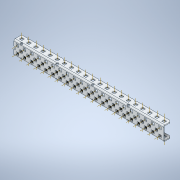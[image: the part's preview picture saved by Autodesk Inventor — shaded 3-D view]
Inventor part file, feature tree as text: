
AUTODESK INVENTOR PART (.ipt)
format: ipt  version: 2020 (Build 240168000, 168)  size: 1,398,784 bytes
history: native  units: in
note: dims shown in document units (in); Inventor stores cm internally (conversion verified against a paired STEP export)
features: other x108, plane x8, pattern_linear x4, split x2, sheet_metal_op x1
ambient origin geometry x8: Origin, YZ Plane, XZ Plane, XY Plane, X Axis, Y Axis, Z Axis, Center Point
bodies: Solid1 (feature_tree)
feature tree (123):
  other  "Work Axis1"
  pattern_linear  "Rectangular Pattern1"  Count1=21 Spacing1=0.5in
  other  "Work Axis72"
  pattern_linear  "Rectangular Pattern2"  Count1=21 Spacing1=0.5in
  pattern_linear  "Rectangular Pattern3"  Count1=21 Spacing1=0.5in
  other  "Work Axis141"
  pattern_linear  "Rectangular Pattern4"  Count1=20 Spacing1=0.5in
  plane  "Work Plane7"
  split  "Split1"
  plane  "Work Plane8"
  split  "Split2"
  plane  "Work Plane1"
  plane  "Work Plane2"
  other  "Work Point1"
  other  "Work Axis2"
  other  "Work Axis3"
  other  "Work Axis4"
  other  "Work Axis5"
  other  "Work Axis6"
  other  "Work Axis7"
  other  "Work Axis8"
  other  "Work Axis9"
  other  "Work Axis10"
  other  "Work Axis11"
  other  "Work Axis12"
  other  "Work Axis13"
  other  "Work Axis14"
  other  "Work Axis15"
  other  "Work Axis16"
  other  "Work Axis17"
  other  "Work Axis18"
  other  "Work Axis19"
  other  "Work Axis20"
  other  "Work Axis21"
  other  "Work Axis36"
  other  "Work Axis37"
  other  "Work Axis38"
  other  "Work Axis39"
  other  "Work Axis40"
  other  "Work Axis41"
  other  "Work Axis42"
  other  "Work Axis43"
  other  "Work Axis44"
  other  "Work Axis45"
  other  "Work Axis46"
  other  "Work Axis47"
  other  "Work Axis48"
  other  "Work Axis49"
  other  "Work Axis50"
  other  "Work Axis51"
  other  "Work Axis52"
  other  "Work Axis53"
  other  "Work Axis54"
  other  "Work Axis55"
  other  "Work Axis56"
  plane  "Work Plane3"
  plane  "Work Plane4"
  other  "Work Point2"
  other  "Work Axis71"
  other  "Work Point3"
  other  "Work Axis73"
  other  "Work Axis74"
  other  "Work Axis75"
  other  "Work Axis76"
  other  "Work Axis77"
  other  "Work Axis78"
  other  "Work Axis79"
  other  "Work Axis80"
  other  "Work Axis81"
  other  "Work Axis82"
  other  "Work Axis83"
  other  "Work Axis84"
  other  "Work Axis85"
  other  "Work Axis86"
  other  "Work Axis87"
  other  "Work Axis88"
  other  "Work Axis89"
  other  "Work Axis90"
  other  "Work Axis91"
  other  "Work Axis92"
  other  "Work Axis107"
  other  "Work Axis108"
  other  "Work Axis109"
  other  "Work Axis110"
  other  "Work Axis111"
  other  "Work Axis112"
  other  "Work Axis113"
  other  "Work Axis114"
  other  "Work Axis115"
  other  "Work Axis116"
  other  "Work Axis117"
  other  "Work Axis118"
  other  "Work Axis119"
  other  "Work Axis120"
  other  "Work Axis121"
  other  "Work Axis122"
  other  "Work Axis123"
  other  "Work Axis124"
  other  "Work Axis125"
  other  "Work Axis126"
  plane  "Work Plane5"
  plane  "Work Plane6"
  other  "Work Point4"
  other  "Work Axis142"
  other  "Work Axis143"
  other  "Work Axis144"
  other  "Work Axis145"
  other  "Work Axis146"
  other  "Work Axis147"
  other  "Work Axis148"
  other  "Work Axis149"
  other  "Work Axis150"
  other  "Work Axis151"
  other  "Work Axis152"
  other  "Work Axis153"
  other  "Work Axis154"
  other  "Work Axis155"
  other  "Work Axis156"
  other  "Work Axis157"
  other  "Work Axis158"
  other  "Work Axis159"
  other  "Work Axis160"
  sheet_metal_op  "Fold1"
